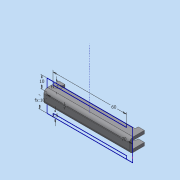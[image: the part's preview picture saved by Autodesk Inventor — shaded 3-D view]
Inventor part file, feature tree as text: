
AUTODESK INVENTOR PART (.ipt)
format: ipt  version: 2020 (Build 240168000, 168)  size: 161,280 bytes
history: native  units: mm
features: other x3, extrude x1
ambient origin geometry x8: Origin, YZ Plane, XZ Plane, XY Plane, X Axis, Y Axis, Z Axis, Center Point
bodies: Body1 (feature_tree)
feature tree (4):
  other  "實體1"
  extrude  "擠出1"  Depth=70.0mm
  other  "折彎零件1"
  other  "折彎零件3"
